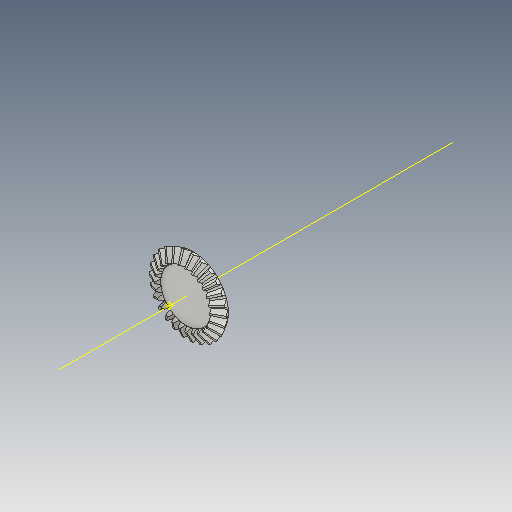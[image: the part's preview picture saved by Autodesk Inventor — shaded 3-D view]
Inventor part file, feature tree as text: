
AUTODESK INVENTOR PART (.ipt)
format: ipt  version: 2021 (Build 250183000, 183)  size: 536,064 bytes
history: native  units: mm
features: other x16, sketch x9, loft x3, pattern_circular x3
ambient origin geometry x6: Origin, XZ Plane, X Axis, Y Axis, Z Axis, Center Point
bodies: Solid1 (feature_tree)
feature tree (31):
  other  "Ponto superior"
  other  "Plano de malha 2"
  other  "Corpo dentado"
  other  "Ponto inicial"
  other  "Plano de dente"
  sketch  "Esboço inicial"  dims[d2=9.449806mm]
  other  "Extremidade"
  loft  "Loft"
  pattern_circular  "Circular Pattern"  [2 undecoded]
  sketch  "Esboço 3D direito"  dims[d3=1.5mm]
  other  "Plano final direito"
  loft  "Transição direita"
  pattern_circular  "Padrão circular direito"  [2 undecoded]
  sketch  "Esboço 3D esquerdo"  dims[d4=2.321835mm]
  other  "Plano final esquerdo"
  loft  "Transição esquerda"
  pattern_circular  "Padrão circular esquerdo"  Count=26 Angle=90.0deg
  other  "Fixar corpo"
  other  "Plano de malha"
  other  "Plano superior"
  sketch  "Esboço de corpo dentado"  dims[d5=90.0deg]
  other  "Plano final"
  sketch  "Esboço final"  dims[d7=3.234854mm]
  other  "Helical Curve Left"
  sketch  "Esboço final esquerdo"  dims[d8=3.288498mm]
  sketch  "Esboço de corpo"  dims[d9=7.917349mm]
  sketch  "Sketch6"  dims[d0=9.1mm d1=8.680233mm]
  other  "Srf1"
  other  "Helical Curve Right"
  sketch  "Esboço final direita"  dims[d11=1.5385mm d12=2.287414mm d15=2.325346mm d16=5.598477mm d17=0.0mm d18=90.0deg d19=0.0mm d20=90.0deg d21=260.0mm d22=360.0deg d26=33.647101mm d27=0.768823mm d28=9.1mm d29=-10.47518mm d30=2.287414mm d31=2.325346mm d32=5.598477mm d35=0.0mm d37=0.0mm d39=0.0mm d40=90.0deg d41=260.0mm d42=360.0deg d46=90.0deg d47=90.0deg d48=0.0mm d49=0.0mm d50=90.0deg d51=1.208305mm d52=0.0mm d53=0.0mm d54=0.0mm d56=1.693245mm d57=9.686054mm d58=8.592654mm d59=6.849155mm d60=6.075995mm d61=6.849155mm d62=6.075995mm d65=33.647101mm d66=31.5mm d67=9.1mm d68=-10.47518mm d69=0.768823mm d70=2.325346mm d71=5.598477mm d72=2.287414mm d73=6.075995mm d74=6.849155mm d75=0.0mm d77=0.0mm d79=0.0mm d80=90.0deg d81=260.0mm d82=360.0deg d84=10.0mm d85=20.0mm d86=20.0mm d87=10.0mm d88=0.0mm d89=0.0mm d90=90.0deg d91=90.0deg d92=90.0deg d93=90.0deg]
  other  "Diâmetro do flanco"
note: 4 required parameter values undecoded (feature->parameter linkage not recoverable at this tier; creation-order binding heuristic only, values carry confidence <= 0.55)
